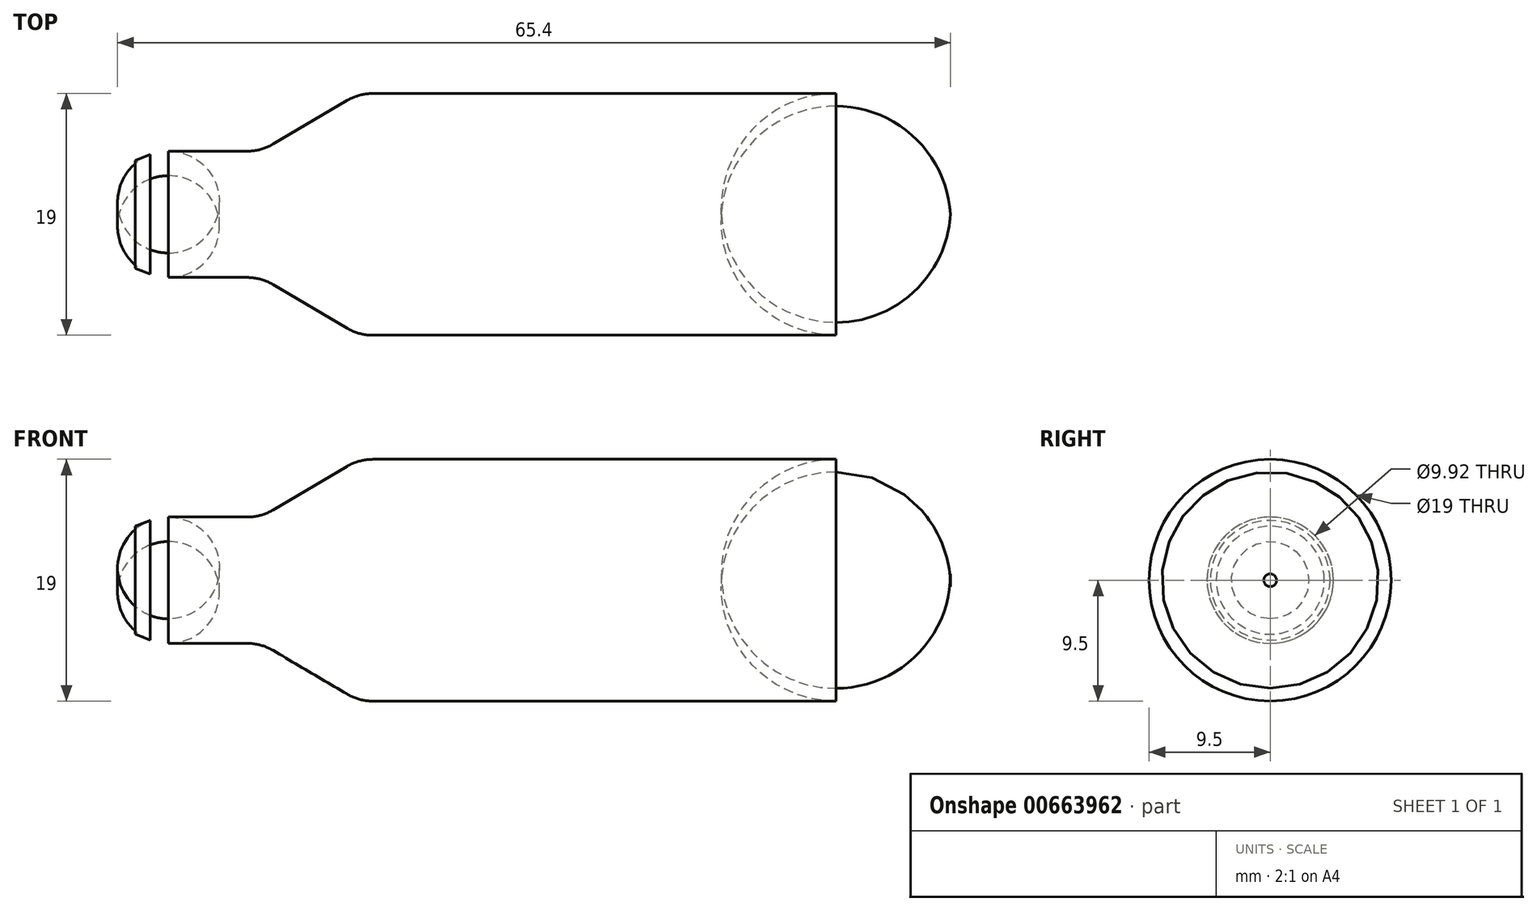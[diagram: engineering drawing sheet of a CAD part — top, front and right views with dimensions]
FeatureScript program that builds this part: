
annotation { "Feature Type Name" : "Feature", "Feature Type Description" : "" }
export const myFeature = defineFeature(function(context is Context, id is Id, definition is map)
    precondition{}
    {
        {
            var Q0;
            Q0=qCreatedBy(makeId("Front.planeOp"),FACE);
            var sketch = newSketch(context, id + "F0", { "sketchPlane" : qUnion([Q0])});
            skLineSegment(sketch, "E0", {"start": v(0, 0) * mm, "end": v(64, 0) * mm});
            skLineSegment(sketch, "E1", {"start": v(64, 0) * mm, "end": v(64, 9.5) * mm});
            skLineSegment(sketch, "E2", {"start": v(0, 0) * mm, "end": v(0, 1.82) * mm});
            skLineSegment(sketch, "E3", {"start": v(0, 0) * mm, "end": v(0, 4.24) * mm});
            skLineSegment(sketch, "E4", {"start": v(0, 4.24) * mm, "end": v(1.87, 4.96) * mm});
            skLineSegment(sketch, "E5", {"start": v(1.87, 4.96) * mm, "end": v(9.87, 4.96) * mm});
            skLineSegment(sketch, "E6", {"start": v(57.57, 9.5) * mm, "end": v(17.57, 9.5) * mm});
            skLineSegment(sketch, "E7", {"start": v(17.57, 9.5) * mm, "end": v(9.87, 4.96) * mm});
            skLineSegment(sketch, "E8", {"start": v(57.57, 9.5) * mm, "end": v(64, 9.5) * mm});
            skSolve(sketch);
        }
        {
            var Q0;
            Q0 = qSketchRegion(id + "F0", true);
            var Q1;
            Q1=sQuery(id+"F0.wireOp",EDGE,"E0");
            revolve(context, id + "F1", {"entities" : qUnion([Q0]), "axis" : qUnion([Q1]), "revolveType" : RevolveType.FULL});
        }
        {
            var Q0;
            Q0=makeQuery(id+"F1.opRevolve","SWEPT_FACE",FACE,{"disambiguationData":[OSD([sQuery(id+"F0.wireOp",EDGE,"E1")])]});
            fillet(context, id + "F2", {"entities" : qUnion([Q0]), "radius" : 9 * mm, "tangentPropagation" : true, "allowEdgeOverflow" : false});
        }
        {
            var Q0;
            Q0=makeQuery(id+"F1.opRevolve","SWEPT_EDGE",EDGE,{"disambiguationData":[OSD([sQuery(id+"F0.wireOp",EDGE,"E6"),sQuery(id+"F0.wireOp",EDGE,"E7")])]});
            var Q1;
            Q1=makeQuery(id+"F1.opRevolve","SWEPT_EDGE",EDGE,{"disambiguationData":[OSD([sQuery(id+"F0.wireOp",EDGE,"E5"),sQuery(id+"F0.wireOp",EDGE,"E7")])]});
            var Q2;
            Q2=makeQuery(id+"F1.opRevolve","SWEPT_EDGE",EDGE,{"disambiguationData":[OSD([sQuery(id+"F0.wireOp",EDGE,"E4"),sQuery(id+"F0.wireOp",EDGE,"E5")])]});
            fillet(context, id + "F3", {"entities" : qUnion([Q0, Q1, Q2]), "radius" : 4 * mm, "tangentPropagation" : true, "allowEdgeOverflow" : false});
        }
    });
